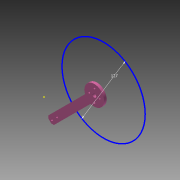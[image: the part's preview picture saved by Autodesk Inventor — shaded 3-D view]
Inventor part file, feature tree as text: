
AUTODESK INVENTOR PART (.ipt)
format: ipt  version: 2015 (Build 190159000, 159)  size: 102,912 bytes
history: native  units: mm
features: other x2, extrude x1, sketch x1
ambient origin geometry x8: Origin, YZ Plane, XZ Plane, XY Plane, X Axis, Y Axis, Z Axis, Center Point
bodies: Body1 (feature_tree)
feature tree (4):
  extrude  "Extrusion3"  Depth=3.0mm
  other  "Motor Simulering"
  other  "Propeller"
  sketch  "Sketch1"  dims[d2=3.0mm d3=3.0mm d4=3.0mm d6=6.0mm d10=2.0mm d23=4.0mm d24=0.0mm d25=10.0mm d26=127.0mm]
